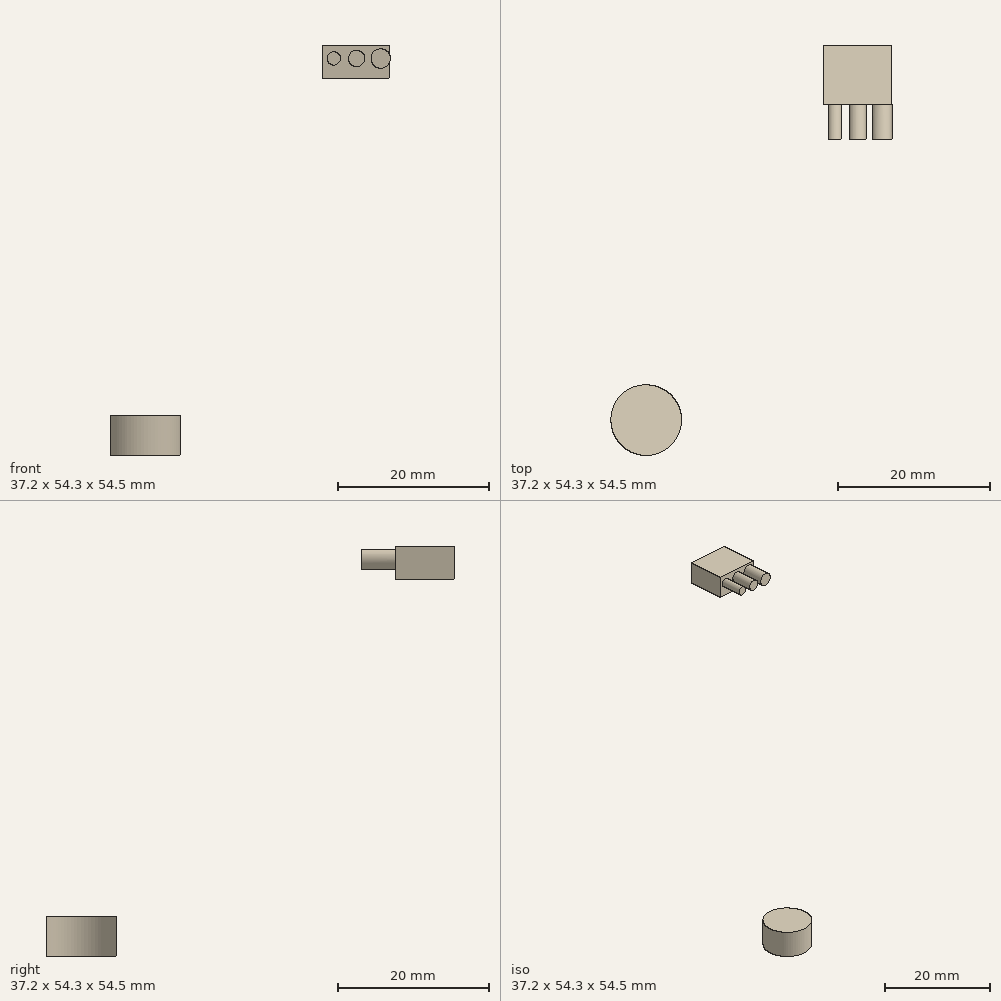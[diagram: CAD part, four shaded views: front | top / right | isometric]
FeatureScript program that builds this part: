
annotation { "Feature Type Name" : "Feature", "Feature Type Description" : "" }
export const myFeature = defineFeature(function(context is Context, id is Id, definition is map)
    precondition{}
    {
        {
            var Q0;
            Q0=qCreatedBy(makeId("Top.planeOp"),FACE);
            var sketch = newSketch(context, id + "F0", { "sketchPlane" : qUnion([Q0])});
            skCircle(sketch, "E0", {"center": v(-142.63, -49.59) * mm, "radius": 4.68 * mm});
            skSolve(sketch);
        }
        {
            var Q0;
            Q0=makeQuery(id+"F0.imprint","IMPRINT",FACE,{"disambiguationData":[TD([[makeQuery(id+"F0.imprint","IMPRINT",EDGE,{"derivedFrom":sQuery(id+"F0.wireOp",EDGE,"E0")}),1.0]])]});
            extrude(context, id + "F1", {"entities" : qUnion([Q0]), "oppositeDirection" : true, "depth" : 5.33 * mm, "offsetDistance" : 25.4 * mm});
        }
        {
            var Q0;
            Q0=qCreatedBy(makeId("Front.planeOp"),FACE);
            var sketch = newSketch(context, id + "F2", { "sketchPlane" : qUnion([Q0])});
            skLineSegment(sketch, "E1.bottom", {"start": v(-119.1, 44.67) * mm, "end": v(-110.2, 44.67) * mm});
            skLineSegment(sketch, "E1.top", {"start": v(-119.1, 49.12) * mm, "end": v(-110.2, 49.12) * mm});
            skLineSegment(sketch, "E1.left", {"start": v(-119.1, 44.67) * mm, "end": v(-119.1, 49.12) * mm});
            skLineSegment(sketch, "E1.right", {"start": v(-110.2, 44.67) * mm, "end": v(-110.2, 49.12) * mm});
            skSolve(sketch);
        }
        {
            var Q0;
            Q0=makeQuery(id+"F2.imprint","IMPRINT",FACE,{"disambiguationData":[TD([[makeQuery(id+"F2.imprint","IMPRINT",EDGE,{"derivedFrom":sQuery(id+"F2.wireOp",EDGE,"E1.bottom")}),1.0]])]});
            extrude(context, id + "F3", {"entities" : qUnion([Q0]), "depth" : 7.87 * mm, "offsetDistance" : 25.4 * mm});
        }
        {
            var Q0;
            Q0=makeQuery(id+"F3.opExtrude","CAP_FACE",FACE,{"disambiguationData":[OSD([sQuery(id+"F2.wireOp",EDGE,"E1.bottom"),sQuery(id+"F2.wireOp",EDGE,"E1.top"),sQuery(id+"F2.wireOp",EDGE,"E1.left"),sQuery(id+"F2.wireOp",EDGE,"E1.right")])],"isStart":false});
            cPlane(context, id + "F4", {"entities" : qUnion([Q0]), "cplaneType" : CPlaneType.OFFSET, "offset" : 0 * mm, "width" : 152.4 * mm, "height" : 152.4 * mm});
        }
        {
            var Q0;
            Q0=qCreatedBy(id+"F4.planeOp",FACE);
            var sketch = newSketch(context, id + "F5", { "sketchPlane" : qUnion([Q0])});
            skCircle(sketch, "E2", {"center": v(-117.6, 47.38) * mm, "radius": 0.89 * mm});
            skCircle(sketch, "E3", {"center": v(-114.59, 47.38) * mm, "radius": 1.08 * mm});
            skCircle(sketch, "E4", {"center": v(-111.39, 47.38) * mm, "radius": 1.3 * mm});
            skSolve(sketch);
        }
        {
            var Q0;
            Q0=makeQuery(id+"F5.imprint","IMPRINT",FACE,{"disambiguationData":[TD([[makeQuery(id+"F5.imprint","IMPRINT",EDGE,{"derivedFrom":sQuery(id+"F5.wireOp",EDGE,"E2")}),1.0]])]});
            var Q1;
            Q1=makeQuery(id+"F5.imprint","IMPRINT",FACE,{"disambiguationData":[TD([[makeQuery(id+"F5.imprint","IMPRINT",EDGE,{"derivedFrom":sQuery(id+"F5.wireOp",EDGE,"E3")}),1.0]])]});
            var Q2;
            Q2=makeQuery(id+"F5.imprint","IMPRINT",FACE,{"disambiguationData":[TD([[makeQuery(id+"F5.imprint","IMPRINT",EDGE,{"derivedFrom":sQuery(id+"F5.wireOp",EDGE,"E4")}),1.0]])]});
            extrude(context, id + "F6", {"entities" : qUnion([Q0, Q1, Q2]), "operationType" : NewBodyOperationType.ADD, "depth" : 4.57 * mm, "offsetDistance" : 25.4 * mm});
        }
    });
